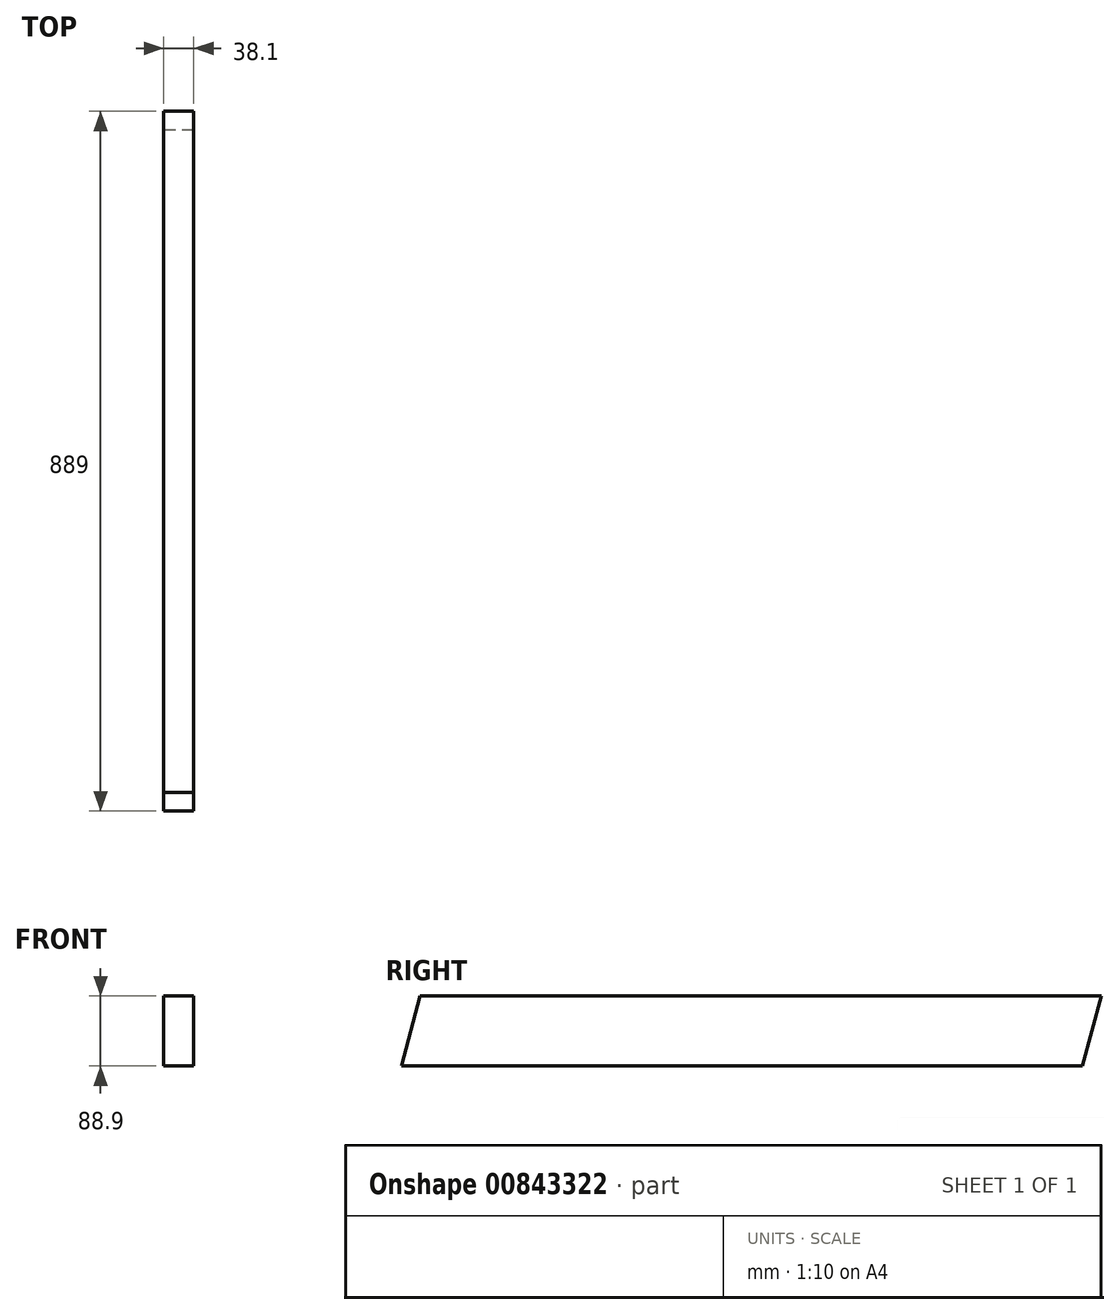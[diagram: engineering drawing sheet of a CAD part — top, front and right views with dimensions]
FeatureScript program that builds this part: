
annotation { "Feature Type Name" : "Feature", "Feature Type Description" : "" }
export const myFeature = defineFeature(function(context is Context, id is Id, definition is map)
    precondition{}
    {
        {
            var Q0;
            Q0=qCreatedBy(makeId("Front.planeOp"),FACE);
            var sketch = newSketch(context, id + "F0", { "sketchPlane" : qUnion([Q0])});
            skLineSegment(sketch, "E0.bottom", {"start": v(19.05, -44.45) * mm, "end": v(-19.05, -44.45) * mm});
            skLineSegment(sketch, "E0.top", {"start": v(19.05, 44.45) * mm, "end": v(-19.05, 44.45) * mm});
            skLineSegment(sketch, "E0.left", {"start": v(19.05, -44.45) * mm, "end": v(19.05, 44.45) * mm});
            skLineSegment(sketch, "E0.right", {"start": v(-19.05, -44.45) * mm, "end": v(-19.05, 44.45) * mm});
            skPoint(sketch, "E0.middle", {"position": v(0, 0) * mm});
            skSolve(sketch);
        }
        {
            var Q0;
            Q0=makeQuery(id+"F0.imprint","IMPRINT",FACE,{"disambiguationData":[TD([[makeQuery(id+"F0.imprint","IMPRINT",EDGE,{"derivedFrom":sQuery(id+"F0.wireOp",EDGE,"E0.bottom")}),-1.0]])]});
            extrude(context, id + "F1", {"entities" : qUnion([Q0]), "depth" : 889 * mm, "offsetDistance" : 25.4 * mm});
        }
        {
            var Q0;
            Q0=qCreatedBy(makeId("Right.planeOp"),FACE);
            var sketch = newSketch(context, id + "F2", { "sketchPlane" : qUnion([Q0])});
            skLineSegment(sketch, "E1", {"start": v(-865.12, 44.45) * mm, "end": v(-889, 44.45) * mm});
            skLineSegment(sketch, "E2", {"start": v(-889, 44.45) * mm, "end": v(-889, -44.45) * mm});
            skLineSegment(sketch, "E3", {"start": v(-889, -44.45) * mm, "end": v(-865.12, 44.45) * mm});
            skSolve(sketch);
        }
        {
            var Q0;
            Q0=qSketchRegion(id+"F2",true);
            extrude(context, id + "F3", {"entities" : qUnion([Q0]), "operationType" : NewBodyOperationType.REMOVE, "oppositeDirection" : true, "depth" : 50.8 * mm, "offsetDistance" : 25.4 * mm, "symmetric" : true});
        }
        {
            var Q0;
            Q0=qCreatedBy(makeId("Right.planeOp"),FACE);
            var sketch = newSketch(context, id + "F4", { "sketchPlane" : qUnion([Q0])});
            skLineSegment(sketch, "E4", {"start": v(0, 44.45) * mm, "end": v(-23.88, -44.45) * mm});
            skLineSegment(sketch, "E5", {"start": v(-23.88, -44.45) * mm, "end": v(0, -44.45) * mm});
            skLineSegment(sketch, "E6", {"start": v(0, -44.45) * mm, "end": v(0, 44.45) * mm});
            skSolve(sketch);
        }
        {
            var Q0;
            Q0=qSketchRegion(id+"F4",true);
            extrude(context, id + "F5", {"entities" : qUnion([Q0]), "operationType" : NewBodyOperationType.REMOVE, "depth" : 50.8 * mm, "offsetDistance" : 25.4 * mm, "symmetric" : true});
        }
    });
